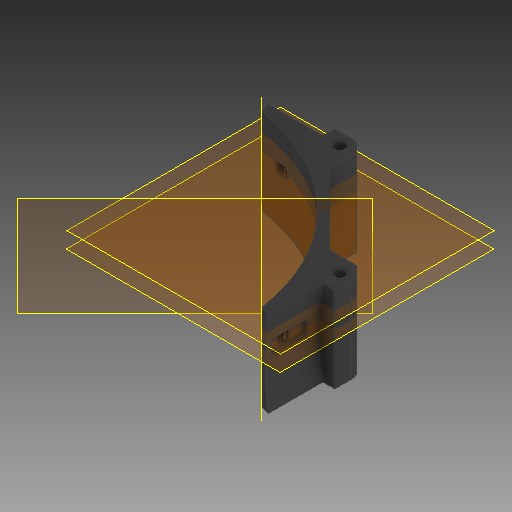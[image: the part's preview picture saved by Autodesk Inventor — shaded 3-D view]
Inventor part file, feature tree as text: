
AUTODESK INVENTOR PART (.ipt)
format: ipt  version: 2020 (Build 240168000, 168)  size: 253,440 bytes
history: native  units: mm
features: sketch x10, extrude x6, other x5, hole x3, mirror x1
ambient origin geometry x8: Origin, YZ Plane, XZ Plane, XY Plane, X Axis, Y Axis, Z Axis, Center Point
bodies: Body1 (feature_tree)
feature tree (25):
  other  "Твердое тело1"
  sketch  "Эскиз1"
  extrude  "Выдавливание1"  Depth=9.0mm
  other  "РабПлоскость1"
  extrude  "Выдавливание2"  Depth=9.0mm
  extrude  "Выдавливание3"  Depth=32.0mm TaperAngle=0.0deg
  other  "РабПлоскость2"
  mirror  "Зеркальное отражение1"
  other  "РабПлоскость3"
  hole  "Отверстие1"  [1 undecoded]
  extrude  "Выдавливание4"  Depth=20.6mm TaperAngle=0.0deg
  other  "РабПлоскость4"
  sketch  "Эскиз9"
  extrude  "Выдавливание6"  Depth=20.5mm TaperAngle=0.0deg
  extrude  "Выдавливание7"  Depth=3.0mm
  hole  "Отверстие2"  [1 undecoded]
  hole  "Отверстие3"  [1 undecoded]
  sketch  "Эскиз2"
  sketch  "Эскиз3"
  sketch  "Эскиз4"
  sketch  "Эскиз6"
  sketch  "Эскиз7"
  sketch  "Эскиз10"
  sketch  "Эскиз11"
  sketch  "Эскиз12"
note: 3 required parameter values undecoded (feature->parameter linkage not recoverable at this tier; creation-order binding heuristic only, values carry confidence <= 0.55)
